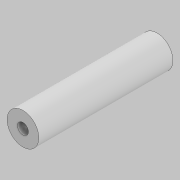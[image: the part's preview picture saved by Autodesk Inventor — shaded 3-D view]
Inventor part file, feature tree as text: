
AUTODESK INVENTOR PART (.ipt)
format: ipt  version: 2021 (Build 250183000, 183)  size: 81,920 bytes
history: native  units: in
note: dims shown in document units (in); Inventor stores cm internally (conversion verified against a paired STEP export)
features: extrude x2, sketch x2
ambient origin geometry x8: Origin, YZ Plane, XZ Plane, XY Plane, X Axis, Y Axis, Z Axis, Center Point
bodies: Solid1 (feature_tree)
feature tree (4):
  extrude  "Extrusion1"  Depth=1.4764in TaperAngle=0.0deg
  extrude  "Extrusion2"  TaperAngle=0.0deg  [1 undecoded]
  sketch  "Sketch1"  dims[d0=0.35in d1=1.4764in d2=0.0in]
  sketch  "Sketch2"  dims[d3=0.12in d4=0.0in d5=0.0in]
note: 1 required parameter value undecoded (feature->parameter linkage not recoverable at this tier; creation-order binding heuristic only, values carry confidence <= 0.55)
